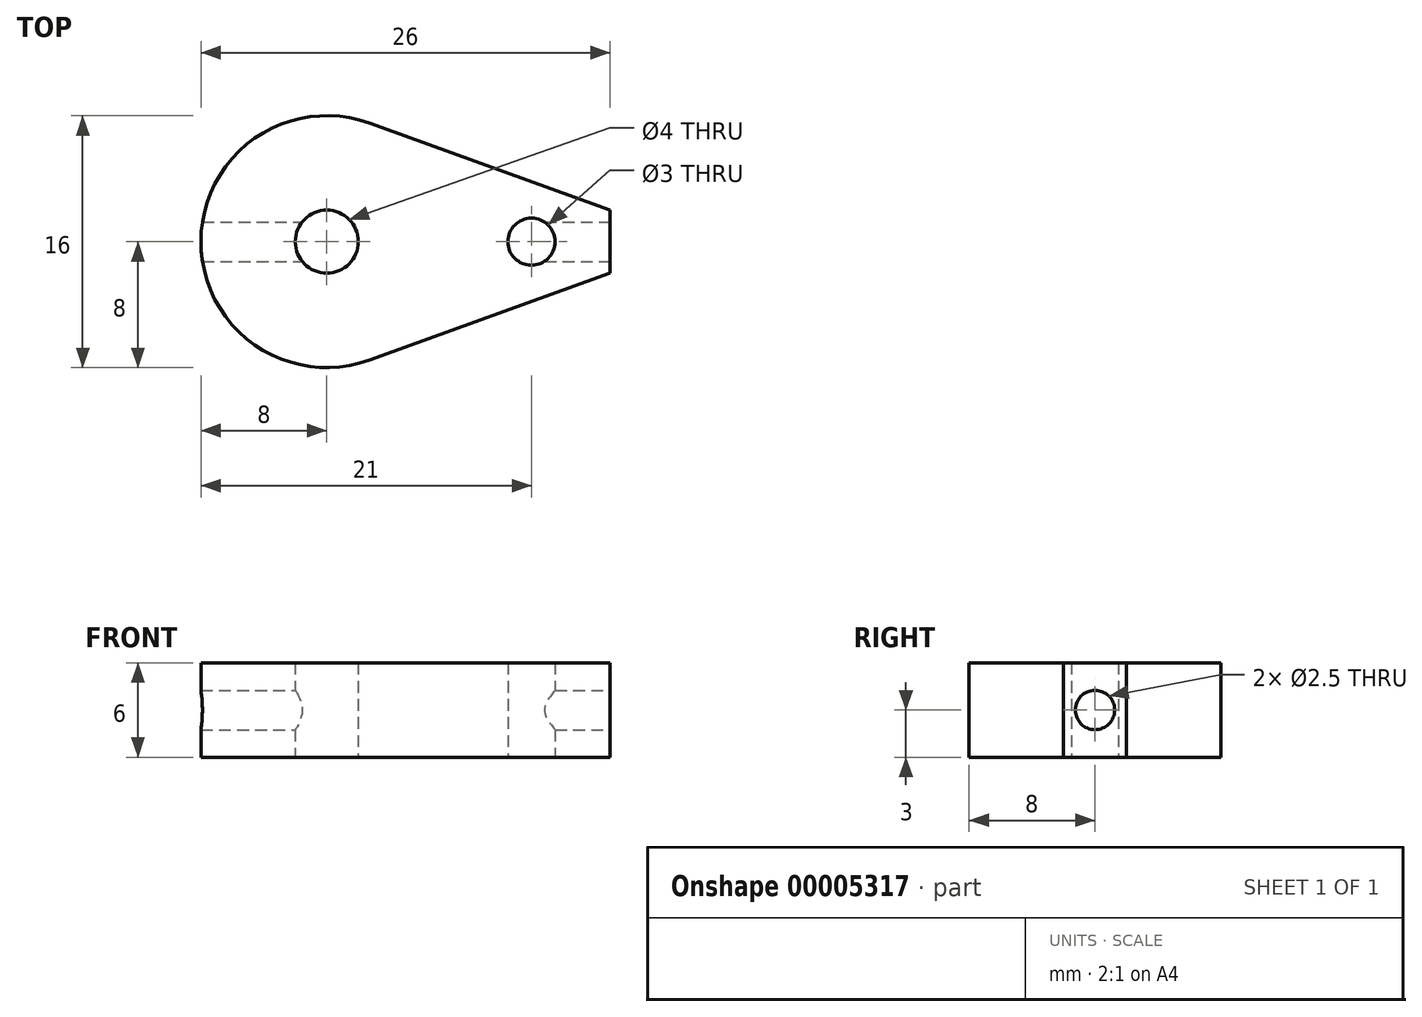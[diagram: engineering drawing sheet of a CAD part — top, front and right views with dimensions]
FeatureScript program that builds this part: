
annotation { "Feature Type Name" : "Feature", "Feature Type Description" : "" }
export const myFeature = defineFeature(function(context is Context, id is Id, definition is map)
    precondition{}
    {
        {
            var Q0;
            Q0=qCreatedBy(makeId("Top.planeOp"),FACE);
            var sketch = newSketch(context, id + "F0", { "sketchPlane" : qUnion([Q0])});
            skArc(sketch, "E0", {"start": v(2.72, 7.52) * mm, "mid": v(-8, 0) * mm, "end": v(2.72, -7.52) * mm});
            skCircle(sketch, "E1", {"center": v(0, 0) * mm, "radius": 2 * mm});
            skCircle(sketch, "E2", {"center": v(13, 0) * mm, "radius": 1.5 * mm});
            skLineSegment(sketch, "E3", {"start": v(18, 0) * mm, "end": v(18, 2) * mm});
            skLineSegment(sketch, "E4", {"start": v(18, 2) * mm, "end": v(18, -2) * mm});
            skLineSegment(sketch, "E5", {"start": v(18, -2) * mm, "end": v(2.72, -7.52) * mm});
            skLineSegment(sketch, "E6", {"start": v(18, 2) * mm, "end": v(2.72, 7.52) * mm});
            skSolve(sketch);
        }
        {
            var Q0;
            Q0=makeQuery(id+"F0.imprint","IMPRINT",FACE,{"disambiguationData":[TD([[makeQuery(id+"F0.imprint","IMPRINT",EDGE,{"derivedFrom":sQuery(id+"F0.wireOp",EDGE,"E0")}),1.0]])]});
            extrude(context, id + "F1", {"entities" : qUnion([Q0]), "depth" : 6 * mm});
        }
        {
            var Q0;
            Q0=makeQuery(id+"F1.opExtrude","SWEPT_FACE",FACE,{"disambiguationData":[OSD([sQuery(id+"F0.wireOp",EDGE,"E4")])]});
            var sketch = newSketch(context, id + "F2", { "sketchPlane" : qUnion([Q0])});
            skCircle(sketch, "E7", {"center": v(0, 3) * mm, "radius": 1.25 * mm});
            skSolve(sketch);
        }
        {
            var Q0;
            Q0=makeQuery(id+"F2.imprint","IMPRINT",FACE,{"disambiguationData":[TD([[makeQuery(id+"F2.imprint","IMPRINT",EDGE,{"derivedFrom":sQuery(id+"F2.wireOp",EDGE,"E7")}),1.0]])]});
            extrude(context, id + "F3", {"entities" : qUnion([Q0]), "operationType" : NewBodyOperationType.REMOVE, "endBound" : BoundingType.UP_TO_NEXT, "oppositeDirection" : true, "depth" : 25 * mm});
        }
        {
            var Q0;
            Q0=qCreatedBy(makeId("Right.planeOp"),FACE);
            var sketch = newSketch(context, id + "F4", { "sketchPlane" : qUnion([Q0])});
            skCircle(sketch, "E8", {"center": v(0, 3) * mm, "radius": 1.25 * mm});
            skSolve(sketch);
        }
        {
            var Q0;
            Q0=makeQuery(id+"F4.imprint","IMPRINT",FACE,{"disambiguationData":[TD([[makeQuery(id+"F4.imprint","IMPRINT",EDGE,{"derivedFrom":sQuery(id+"F4.wireOp",EDGE,"E8")}),1.0]])]});
            var Q1;
            Q1=sQuery(id+"F4.wireOp",EDGE,"E8");
            extrude(context, id + "F5", {"entities" : qUnion([Q0]), "operationType" : NewBodyOperationType.REMOVE, "surfaceEntities" : qUnion([Q1]), "oppositeDirection" : true, "depth" : 25 * mm});
        }
    });
